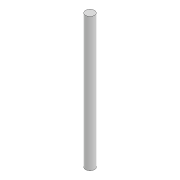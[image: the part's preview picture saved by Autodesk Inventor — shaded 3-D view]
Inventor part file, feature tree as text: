
AUTODESK INVENTOR PART (.ipt)
format: ipt  version: 2021 (Build 250183000, 183)  size: 70,144 bytes
history: native  units: in
note: dims shown in document units (in); Inventor stores cm internally (conversion verified against a paired STEP export)
features: extrude x1, sketch x1
ambient origin geometry x8: Origin, YZ Plane, XZ Plane, XY Plane, X Axis, Y Axis, Z Axis, Center Point
bodies: Solid1 (feature_tree)
feature tree (2):
  extrude  "Extrusion1"  Depth=118.1102in TaperAngle=0.0deg
  sketch  "Sketch1"  dims[d0=7.874in d1=118.1102in d2=0.0in]
